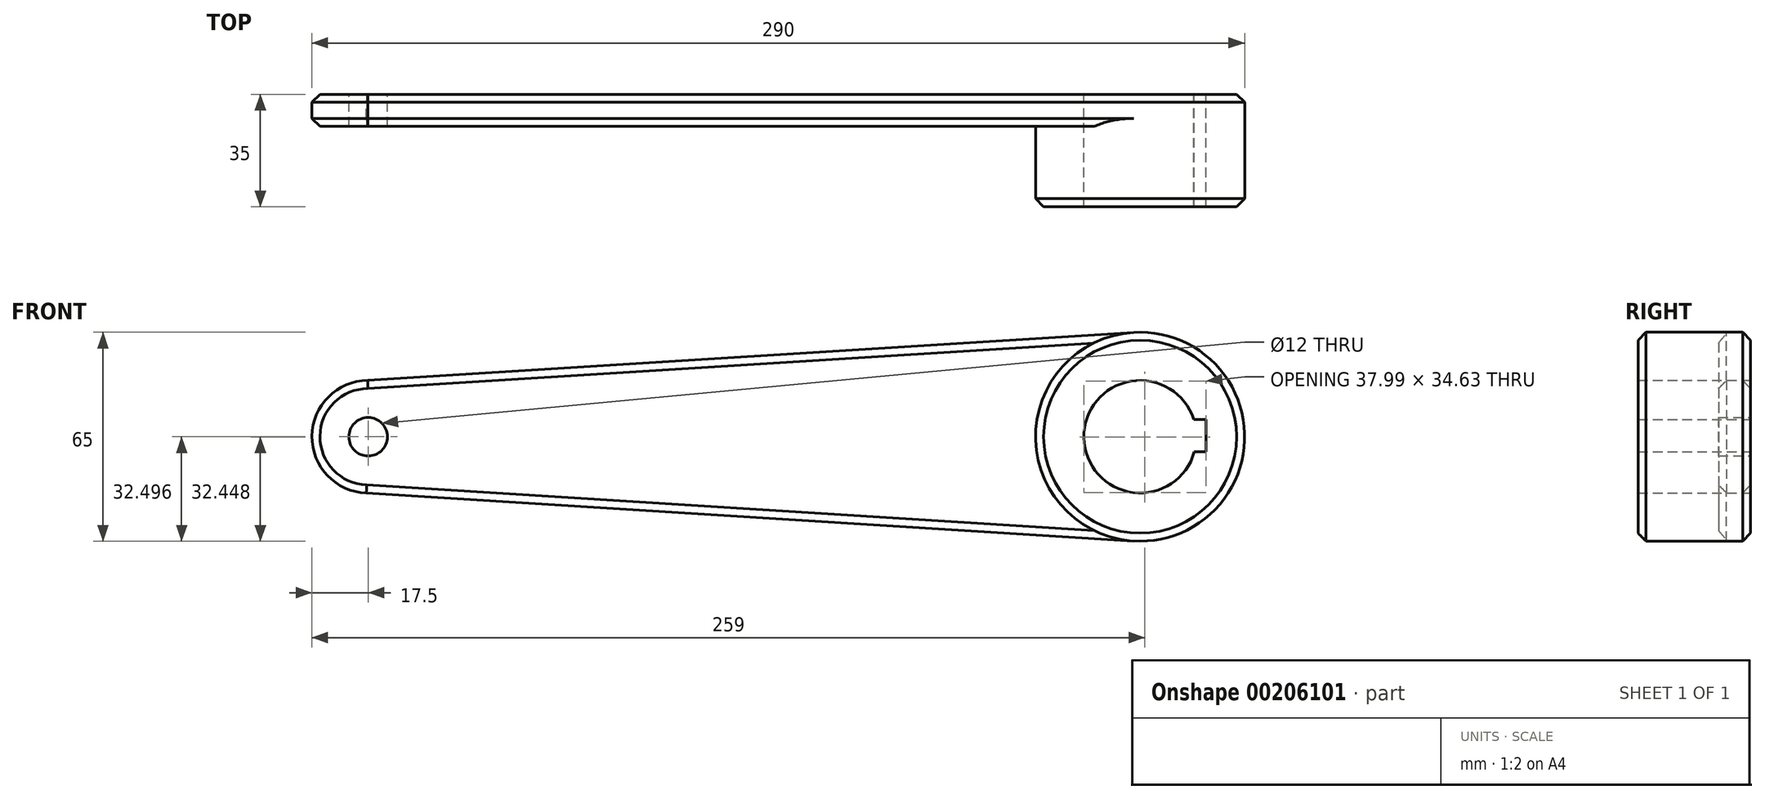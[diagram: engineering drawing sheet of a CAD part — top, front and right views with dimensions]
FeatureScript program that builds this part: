
annotation { "Feature Type Name" : "Feature", "Feature Type Description" : "" }
export const myFeature = defineFeature(function(context is Context, id is Id, definition is map)
    precondition{}
    {
        {
            var Q0;
            Q0=qCreatedBy(makeId("Front.planeOp"),FACE);
            var sketch = newSketch(context, id + "F0", { "sketchPlane" : qUnion([Q0])});
            skCircle(sketch, "E0", {"center": v(-60.07, 0.49) * mm, "radius": 32.5 * mm});
            skLineSegment(sketch, "E1", {"start": v(-60.07, 0.49) * mm, "end": v(-285.3, 0.49) * mm});
            skCircle(sketch, "E2", {"center": v(-300.07, 0.49) * mm, "radius": 17.5 * mm});
            skLineSegment(sketch, "E3", {"start": v(-300.25, 17.98) * mm, "end": v(-62.1, 32.92) * mm});
            skLineSegment(sketch, "E4", {"start": v(-300.65, -17) * mm, "end": v(-62.1, -31.95) * mm});
            skCircle(sketch, "E5", {"center": v(-60.07, 0.49) * mm, "radius": 17.5 * mm});
            skLineSegment(sketch, "E6.bottom", {"start": v(-39.57, -4.2) * mm, "end": v(-45.57, -4.2) * mm});
            skLineSegment(sketch, "E6.top", {"start": v(-39.57, 5.8) * mm, "end": v(-45.57, 5.8) * mm});
            skLineSegment(sketch, "E6.left", {"start": v(-39.57, -4.2) * mm, "end": v(-39.57, 5.8) * mm});
            skLineSegment(sketch, "E6.right", {"start": v(-45.57, -4.2) * mm, "end": v(-45.57, 5.8) * mm});
            skPoint(sketch, "E6.middle", {"position": v(-42.57, 0.8) * mm});
            skPoint(sketch, "E7", {"position": v(-27.57, 0.11) * mm});
            skLineSegment(sketch, "E8", {"start": v(-60.07, 0.49) * mm, "end": v(-331.53, 0.49) * mm});
            skPoint(sketch, "E9", {"position": v(-317.57, 0.49) * mm});
            skSolve(sketch);
        }
        {
            var Q0;
            {var subQ0=sQuery(id+"F0.wireOp",EDGE,"E0");var subQ1=makeQuery(id+"F0.imprint","INTERSECT",VERTEX,{"derivedFrom":[subQ0,sQuery(id+"F0.wireOp",EDGE,"E3")]});Q0=makeQuery(id+"F0.imprint","IMPRINT",FACE,{"disambiguationData":[TD([[makeQuery(id+"F0.imprint","IMPRINT",EDGE,{"disambiguationData":[TD([[subQ1,-1.0]])],"derivedFrom":subQ0}),1.0]])]});}
            extrude(context, id + "F1", {"entities" : qUnion([Q0]), "depth" : 35 * mm});
        }
        {
            var Q0;
            Q0 = qSketchRegion(id + "F0", true);
            extrude(context, id + "F2", {"entities" : qUnion([Q0]), "operationType" : NewBodyOperationType.ADD, "depth" : 10 * mm});
        }
        {
            var Q0;
            Q0=sQuery(id+"F0.wireOp",VERTEX,"E2.center");
            var Q1;
            Q1=makeQuery(id+"F1.opExtrude","SWEPT_BODY",BODY,{"disambiguationData":[OSD([sQuery(id+"F0.wireOp",EDGE,"E0")])]});
            hole(context, id + "F3", {"style" : HoleStyle.SIMPLE, "endStyle" : HoleEndStyle.THROUGH, "oppositeDirection" : true, "holeDiameter" : 12 * mm, "locations" : qUnion([Q0]), "scope" : qUnion([Q1]), "isTappedThrough" : true});
        }
        {
            var Q0;
            Q0=makeQuery(id+"F2.opExtrude","CAP_EDGE",EDGE,{"disambiguationData":[OSD([sQuery(id+"F0.wireOp",EDGE,"E3")])],"isStart":false});
            var Q1;
            Q1=makeQuery(id+"F2.opExtrude","CAP_EDGE",EDGE,{"disambiguationData":[OSD([sQuery(id+"F0.wireOp",EDGE,"E3")])],"isStart":true});
            var Q2;
            Q2=makeQuery(id+"F2.opExtrude","CAP_EDGE",EDGE,{"disambiguationData":[OSD([sQuery(id+"F0.wireOp",EDGE,"E2")])],"isStart":false});
            var Q3;
            Q3=makeQuery(id+"F2.opExtrude","CAP_EDGE",EDGE,{"disambiguationData":[OSD([sQuery(id+"F0.wireOp",EDGE,"E4")])],"isStart":false});
            var Q4;
            Q4=makeQuery(id+"F1.opExtrude","CAP_EDGE",EDGE,{"disambiguationData":[OSD([sQuery(id+"F0.wireOp",EDGE,"E0")])],"isStart":false});
            var Q5;
            Q5=makeQuery(id+"F1.opExtrude","CAP_EDGE",EDGE,{"disambiguationData":[OSD([sQuery(id+"F0.wireOp",EDGE,"E0")])],"isStart":true});
            var Q6;
            Q6=makeQuery(id+"F2.opExtrude","CAP_EDGE",EDGE,{"disambiguationData":[OSD([sQuery(id+"F0.wireOp",EDGE,"E2")])],"isStart":true});
            var Q7;
            Q7=makeQuery(id+"F2.opExtrude","CAP_EDGE",EDGE,{"disambiguationData":[OSD([sQuery(id+"F0.wireOp",EDGE,"E4")])],"isStart":true});
            chamfer(context, id + "F4", {"entities" : qUnion([Q0, Q1, Q2, Q3, Q4, Q5, Q6, Q7]), "width" : 2.5 * mm, "tangentPropagation" : true});
        }
    });
